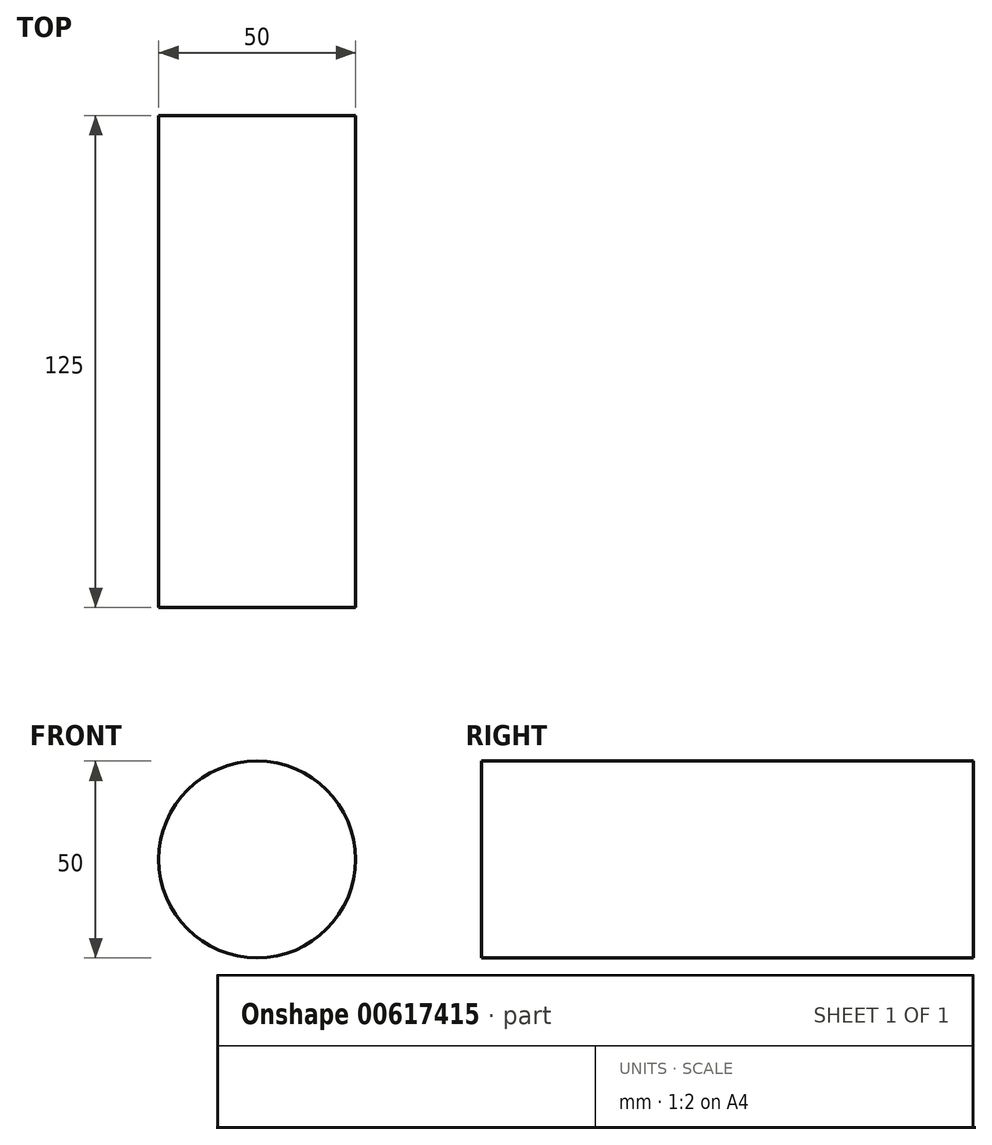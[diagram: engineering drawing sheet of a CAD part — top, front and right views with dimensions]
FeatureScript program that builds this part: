
annotation { "Feature Type Name" : "Feature", "Feature Type Description" : "" }
export const myFeature = defineFeature(function(context is Context, id is Id, definition is map)
    precondition{}
    {
        {
            var Q0;
            Q0=qCreatedBy(makeId("Front.planeOp"),FACE);
            var sketch = newSketch(context, id + "F0", { "sketchPlane" : qUnion([Q0])});
            skCircle(sketch, "E0", {"center": v(0, 0) * mm, "radius": 25 * mm});
            skSolve(sketch);
        }
        {
            var Q0;
            Q0=makeQuery(id+"F0.imprint","IMPRINT",FACE,{"disambiguationData":[TD([[makeQuery(id+"F0.imprint","IMPRINT",EDGE,{"derivedFrom":sQuery(id+"F0.wireOp",EDGE,"E0")}),1.0]])]});
            extrude(context, id + "F1", {"entities" : qUnion([Q0]), "depth" : 100 * mm, "offsetDistance" : 25 * mm});
        }
        {
            var Q0;
            Q0=makeQuery(id+"F1.opExtrude","CAP_FACE",FACE,{"disambiguationData":[OSD([sQuery(id+"F0.wireOp",EDGE,"E0")])],"isStart":false});
            extrude(context, id + "F2", {"entities" : qUnion([Q0]), "operationType" : NewBodyOperationType.ADD, "depth" : 25 * mm, "offsetDistance" : 25 * mm});
        }
    });
